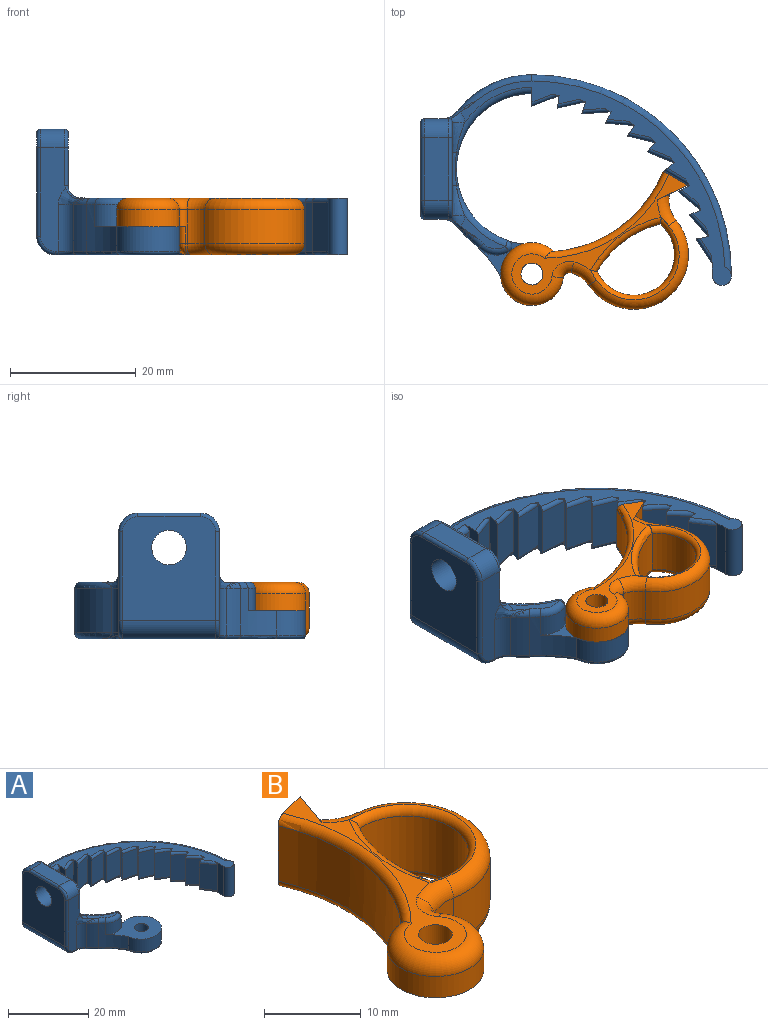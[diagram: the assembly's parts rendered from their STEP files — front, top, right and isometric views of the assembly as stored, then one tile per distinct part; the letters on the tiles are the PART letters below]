
ASSEMBLY  parts=2 mates=1
PART A: 117 faces, bbox 52.8x40.3x23.9 mm
  f0: plane 43.39x32.88mm, normal (0,0,1), area 133.2mm2, adj f5,f7,f8,f10,f11,f13,f14,f16
  f1: plane 16.41x4.05mm, normal (0,-1,0), area 52.5mm2, adj f64,f65,f67,f75,f76,f77,f85,f116
  f2: cylinder r=15mm len=7.4mm, axis (0,0,-1), area 22.7mm2, adj f3,f55,f64,f73
  f3: cylinder r=19.35mm len=7.4mm, axis (0,0,-1), area 35.4mm2, adj f2,f43,f44,f45,f56,f72
  f4: cylinder r=12mm len=23.91mm, axis (0,0,-1), area 259.4mm2, adj f5,f43,f44,f46,f50,f51,f52,f70
  f5: plane 9.1x3.1mm, normal (-1,0,0), area 18.1mm2, adj f0,f4,f6,f41,f50,f70,f98,f108
  f6: plane 7.8x4.3mm, normal (0.36,-0.93,0), area 36mm2, adj f5,f7,f98,f108
  f7: plane 9.44x1.65mm, normal (-0.15,-0.99,0), area 0.5mm2, adj f0,f6,f8,f41,f98,f108
  f8: plane 9.1x2.08mm, normal (-0.99,0.15,0), area 17.8mm2, adj f0,f7,f9,f41,f99,f109
  f9: plane 7.8x4.5mm, normal (0.22,-0.98,0), area 36mm2, adj f8,f10,f99,f109
  f10: plane 9.44x1.61mm, normal (-0.3,-0.95,0), area 0.5mm2, adj f0,f9,f11,f41,f99,f109
  f11: plane 9.1x2.01mm, normal (-0.95,0.3,0), area 17.8mm2, adj f0,f10,f12,f41,f90,f100
  f12: plane 7.8x4.6mm, normal (0.07,-1,0), area 36mm2, adj f11,f13,f90,f100
  f13: plane 9.44x1.54mm, normal (-0.44,-0.9,0), area 0.5mm2, adj f0,f12,f14,f41,f90,f100
  f14: plane 9.1x1.9mm, normal (-0.9,0.44,0), area 17.8mm2, adj f0,f13,f15,f41,f91,f101
  f15: plane 7.8x4.6mm, normal (-0.08,-1,0), area 36mm2, adj f14,f16,f91,f101
  f16: plane 9.44x1.45mm, normal (-0.57,-0.82,0), area 0.5mm2, adj f0,f15,f17,f41,f91,f101
  f17: plane 9.1x1.74mm, normal (-0.82,0.57,0), area 17.8mm2, adj f0,f16,f18,f41,f92,f102
  f18: plane 7.8x4.49mm, normal (-0.23,-0.97,0), area 36mm2, adj f17,f19,f92,f102
  f19: plane 9.44x1.33mm, normal (-0.69,-0.73,0), area 0.5mm2, adj f0,f18,f20,f41,f92,f102
  f20: plane 9.1x1.55mm, normal (-0.73,0.69,0), area 17.8mm2, adj f0,f19,f21,f41,f93,f103
  f21: plane 7.8x4.28mm, normal (-0.38,-0.93,0), area 36mm2, adj f20,f22,f93,f103
  f22: plane 9.44x1.4mm, normal (-0.79,-0.62,0), area 0.5mm2, adj f0,f21,f23,f41,f93,f103
  f23: plane 9.1x1.67mm, normal (-0.62,0.79,0), area 17.8mm2, adj f0,f22,f24,f41,f94,f104
  f24: plane 7.8x3.97mm, normal (-0.51,-0.86,0), area 36mm2, adj f23,f25,f94,f104
  f25: plane 9.44x1.51mm, normal (-0.87,-0.49,0), area 0.5mm2, adj f0,f24,f26,f41,f94,f104
  f26: plane 9.1x1.84mm, normal (-0.49,0.87,0), area 17.8mm2, adj f0,f25,f27,f41,f95,f105
  f27: plane 7.8x3.57mm, normal (-0.63,-0.77,0), area 36mm2, adj f26,f28,f95,f105
  f28: plane 9.44x1.58mm, normal (-0.94,-0.35,0), area 0.5mm2, adj f0,f27,f29,f41,f95,f105
  f29: plane 9.1x1.97mm, normal (-0.35,0.94,0), area 17.8mm2, adj f0,f28,f30,f41,f96,f106
  f30: plane 7.8x3.43mm, normal (-0.74,-0.67,0), area 36mm2, adj f29,f31,f96,f106
  f31: plane 9.44x1.64mm, normal (-0.98,-0.21,0), area 0.5mm2, adj f0,f30,f32,f41,f96,f106
  f32: plane 9.1x2.05mm, normal (-0.21,0.98,0), area 17.8mm2, adj f0,f31,f33,f41,f97,f107
  f33: plane 7.8x3.86mm, normal (-0.84,-0.55,0), area 36mm2, adj f32,f34,f97,f107
  f34: cylinder r=28.69mm len=9mm, axis (0,0,-1), area 18.6mm2, adj f0,f33,f35,f41,f97,f107
  f35: cylinder r=1.5mm len=9mm, axis (0,0,-1), area 44.9mm2, adj f0,f34,f36,f41,f57,f59
  f36: cylinder r=31.69mm len=31.94mm, axis (0,0,-1), area 350.2mm2, adj f35,f37,f57,f59
  f37: cylinder r=15mm len=11.87mm, axis (0,0,-1), area 95.9mm2, adj f36,f58,f60,f62
  f38: plane 16.41x4.05mm, normal (0,1,0), area 52.5mm2, adj f61,f62,f63,f68,f81,f82,f83,f89
  f39: plane 16.4x14.8mm, normal (-1,0,0), area 216.5mm2, adj f49,f69,f77,f78,f79,f80,f81
  f40: plane 7.13x5.3mm, normal (0,0,1), area 8.6mm2, adj f52,f54,f56,f65,f66,f115,f116
  f41: plane 46.99x35.7mm, normal (0,0,-1), area 258.7mm2, adj f5,f7,f8,f10,f11,f13,f14,f16
  f42: cylinder r=1.75mm len=4.5mm, axis (0,0,-1), area 49.5mm2, adj f41,f44
  f43: cylinder r=5mm len=10mm, axis (0,0,-1), area 96.1mm2, adj f3,f4,f44,f71
  f44: plane 13.45x10.33mm, normal (0,0,1), area 75.3mm2, adj f3,f4,f42,f43,f45,f46
  f45: cylinder r=4mm len=4.75mm, axis (0,0,-1), area 18mm2, adj f3,f44,f46,f54
  f46: cylinder r=1mm len=3.5mm, axis (0,0,1), area 8.1mm2, adj f4,f44,f45,f53
  f47: plane 14.81x9.44mm, normal (1,0,0), area 105.9mm2, adj f49,f85,f86,f87,f88,f89,f111,f112
  f48: plane 10x3.8mm, normal (0,0,1), area 38mm2, adj f67,f68,f79,f87
  f49: cylinder r=2.75mm len=5.5mm, axis (1,0,0), area 86.4mm2, adj f39,f47
  f50: torus R=13mm, axis (0,0,1), area 24.4mm2, adj f0,f4,f5,f51,f112
  f51: bspline ~6.69x1.16mm, area 3.8mm2, adj f4,f50,f52,f113
  f52: torus R=13mm, axis (0,0,1), area 18mm2, adj f4,f40,f51,f53,f114
  f53: sphere r=1mm, area 1.9mm2, adj f46,f52,f54
  f54: torus R=3mm, axis (0,0,1), area 7.3mm2, adj f40,f45,f53,f56
  f55: torus R=14mm, axis (0,0,1), area 2.2mm2, adj f2,f56,f65
  f56: torus R=20.35mm, axis (0,0,1), area 2.8mm2, adj f3,f40,f54,f55,f66
  f57: torus R=30.69mm, axis (0,0,1), area 76.6mm2, adj f35,f36,f41,f58
  f58: torus R=14mm, axis (0,0,1), area 19.3mm2, adj f37,f41,f57,f63
  f59: torus R=30.69mm, axis (0,0,1), area 76.6mm2, adj f0,f35,f36,f60
  f60: torus R=14mm, axis (0,0,1), area 19.3mm2, adj f0,f37,f59,f61
  f61: bspline ~6.49x4.52mm, area 6.6mm2, adj f0,f38,f60,f62,f110
  f62: cylinder r=3mm len=7mm, axis (0,0,-1), area 19.2mm2, adj f37,f38,f61,f63
  f63: bspline ~6.49x4.52mm, area 1.8mm2, adj f38,f58,f62,f84
  f64: cylinder r=3mm len=7.4mm, axis (0,0,-1), area 20.3mm2, adj f1,f2,f65,f74
  f65: bspline ~5.43x4.74mm, area 5.6mm2, adj f1,f40,f55,f64,f66,f116
  f66: bspline ~3.52x3.49mm, area 0mm2, adj f40,f56,f65
  f67: cylinder r=3mm len=3.8mm, axis (-1,0,0), area 17.9mm2, adj f1,f48,f78,f86
  f68: cylinder r=3mm len=3.8mm, axis (1,0,0), area 17.9mm2, adj f38,f48,f80,f88
  f69: cylinder r=3mm len=14.8mm, axis (0,-1,0), area 69.7mm2, adj f39,f41,f76,f82
  f70: torus R=12.6mm, axis (0,0,1), area 34.8mm2, adj f4,f5,f41,f71
  f71: torus R=4.4mm, axis (0,0,1), area 22.3mm2, adj f41,f43,f70,f72
  f72: torus R=19.95mm, axis (0,0,1), area 7.2mm2, adj f3,f41,f71,f73
  f73: torus R=14.4mm, axis (0,0,1), area 2.8mm2, adj f2,f41,f72,f74
  f74: torus R=3.6mm, axis (0,0,1), area 2.8mm2, adj f41,f64,f73,f75
  f75: cylinder r=0.6mm len=0.6mm, axis (1,0,0), area 0.4mm2, adj f1,f41,f74,f76
  f76: torus R=2.4mm, axis (0,1,0), area 4.1mm2, adj f1,f69,f75,f77
  f77: cylinder r=0.6mm len=14mm, axis (0,0,-1), area 13.2mm2, adj f1,f39,f76,f78
  f78: torus R=2.4mm, axis (1,0,0), area 4.1mm2, adj f39,f67,f77,f79
  f79: cylinder r=0.6mm len=10mm, axis (0,1,0), area 9.4mm2, adj f39,f48,f78,f80
  f80: torus R=2.4mm, axis (1,0,0), area 4.1mm2, adj f39,f68,f79,f81
  f81: cylinder r=0.6mm len=14mm, axis (0,0,1), area 13.2mm2, adj f38,f39,f80,f82
  f82: torus R=2.4mm, axis (0,1,0), area 4.1mm2, adj f38,f69,f81,f83
  f83: cylinder r=0.6mm len=0.6mm, axis (-1,0,0), area 0.4mm2, adj f38,f41,f82,f84
  f84: bspline ~6.37x3.6mm, area 2.3mm2, adj f41,f63,f83
  f85: cylinder r=0.6mm len=6mm, axis (0,0,1), area 5.7mm2, adj f1,f47,f86,f116
  f86: torus R=2.4mm, axis (1,0,0), area 4.1mm2, adj f47,f67,f85,f87
  f87: cylinder r=0.6mm len=10mm, axis (0,-1,0), area 9.4mm2, adj f47,f48,f86,f88
  f88: torus R=2.4mm, axis (1,0,0), area 4.1mm2, adj f47,f68,f87,f89
  f89: cylinder r=0.6mm len=6mm, axis (0,0,-1), area 5.7mm2, adj f38,f47,f88,f110
  f90: cylinder r=0.6mm len=4.65mm, axis (1,0.07,0), area 3.7mm2, adj f11,f12,f13,f41
  f91: cylinder r=0.6mm len=4.65mm, axis (1,-0.08,0), area 3.7mm2, adj f14,f15,f16,f41
  f92: cylinder r=0.6mm len=4.63mm, axis (0.97,-0.23,0), area 3.7mm2, adj f17,f18,f19,f41
  f93: cylinder r=0.6mm len=4.5mm, axis (0.93,-0.38,0), area 3.7mm2, adj f20,f21,f22,f41
  f94: cylinder r=0.6mm len=4.27mm, axis (0.86,-0.51,0), area 3.7mm2, adj f23,f24,f25,f41
  f95: cylinder r=0.6mm len=3.95mm, axis (0.77,-0.63,0), area 3.7mm2, adj f26,f27,f28,f41
  f96: cylinder r=0.6mm len=3.83mm, axis (0.67,-0.74,0), area 3.7mm2, adj f29,f30,f31,f41
  f97: cylinder r=0.6mm len=4.19mm, axis (0.55,-0.84,0), area 3.7mm2, adj f32,f33,f34,f41
  f98: cylinder r=0.6mm len=4.52mm, axis (0.93,0.36,0), area 3.7mm2, adj f5,f6,f7,f41
  f99: cylinder r=0.6mm len=4.63mm, axis (0.98,0.22,0), area 3.7mm2, adj f8,f9,f10,f41
  f100: cylinder r=0.6mm len=4.65mm, axis (-1,-0.07,0), area 3.7mm2, adj f0,f11,f12,f13
  f101: cylinder r=0.6mm len=4.65mm, axis (-1,0.08,0), area 3.7mm2, adj f0,f14,f15,f16
  f102: cylinder r=0.6mm len=4.63mm, axis (-0.97,0.23,0), area 3.7mm2, adj f0,f17,f18,f19
  f103: cylinder r=0.6mm len=4.5mm, axis (-0.93,0.38,0), area 3.7mm2, adj f0,f20,f21,f22
  f104: cylinder r=0.6mm len=4.27mm, axis (-0.86,0.51,0), area 3.7mm2, adj f0,f23,f24,f25
  f105: cylinder r=0.6mm len=3.95mm, axis (-0.77,0.63,0), area 3.7mm2, adj f0,f26,f27,f28
  f106: cylinder r=0.6mm len=3.83mm, axis (-0.67,0.74,0), area 3.7mm2, adj f0,f29,f30,f31
  f107: cylinder r=0.6mm len=4.19mm, axis (-0.55,0.84,0), area 3.7mm2, adj f0,f32,f33,f34
  f108: cylinder r=0.6mm len=4.52mm, axis (-0.93,-0.36,0), area 3.7mm2, adj f0,f5,f6,f7
  f109: cylinder r=0.6mm len=4.63mm, axis (-0.98,-0.22,0), area 3.7mm2, adj f0,f8,f9,f10
  f110: torus R=2.6mm, axis (0,0,1), area 3.4mm2, adj f0,f38,f61,f89,f111
  f111: cylinder r=2mm len=2mm, axis (0,-1,0), area 0mm2, adj f0,f47,f110,f112
  f112: bspline ~5.75x2.29mm, area 11.4mm2, adj f47,f50,f111,f113
  f113: bspline ~6.41x1.62mm, area 7.5mm2, adj f47,f51,f112,f114
  f114: bspline ~6.02x2.3mm, area 11.4mm2, adj f47,f52,f113,f115
  f115: cylinder r=2mm len=2mm, axis (0,-1,0), area 0mm2, adj f40,f47,f114,f116
  f116: torus R=2.6mm, axis (0,0,1), area 3.4mm2, adj f1,f40,f65,f85,f115
PART B: 38 faces, bbox 24.2x33.1x9.1 mm
  f0: cylinder r=20.2mm len=21.49mm, axis (0,0,-1), area 153.2mm2, adj f5,f11,f12,f15,f16,f20,f31,f32
  f1: cylinder r=5mm len=2.7mm, axis (0,0,-1), area 3.7mm2, adj f12,f16,f23,f30
  f2: cylinder r=8.67mm len=17.29mm, axis (0,0,-1), area 151.2mm2, adj f13,f14,f26,f35
  f3: cylinder r=14.41mm len=5.4mm, axis (0,0,-1), area 1.3mm2, adj f4,f13,f24,f37
  f4: plane 9.03x5.04mm, normal (0.94,-0.34,0), area 30.7mm2, adj f3,f5,f8,f9,f24,f25,f36,f37
  f5: plane 9x4.39mm, normal (-0.26,0.97,0), area 40.4mm2, adj f0,f4,f8,f9,f15,f20
  f6: cylinder r=6.42mm len=12.85mm, axis (0,0,-1), area 161.5mm2, adj f7,f18,f21
  f7: cylinder r=16.13mm len=12.39mm, axis (0,0,-1), area 90mm2, adj f6,f19,f22
  f8: plane 30.66x11.39mm, normal (0,0,1), area 54.2mm2, adj f4,f5,f10,f20,f22,f32,f33,f34
  f9: plane 21.47x5.9mm, normal (0,0,-1), area 27mm2, adj f4,f5,f15,f19,f25,f27,f28,f30
  f10: cylinder r=1.75mm len=4.5mm, axis (0,0,-1), area 49.5mm2, adj f8,f12
  f11: cylinder r=5mm len=10mm, axis (0,0,-1), area 72.3mm2, adj f0,f12,f17,f32
  f12: plane 11.31x10mm, normal (0,0,-1), area 69.8mm2, adj f0,f1,f10,f11,f16,f17,f23
  f13: cylinder r=5mm len=5.4mm, axis (0,0,1), area 22.6mm2, adj f2,f3,f25,f36
  f14: cylinder r=5mm len=5.4mm, axis (0,0,1), area 19.2mm2, adj f2,f17,f27,f34
  f15: torus R=21.2mm, axis (0,0,1), area 32.3mm2, adj f0,f5,f9,f31
  f16: cylinder r=1mm len=2.7mm, axis (0,0,-1), area 5.1mm2, adj f0,f1,f12,f31
  f17: cylinder r=1mm len=5.4mm, axis (0,0,-1), area 5.4mm2, adj f11,f12,f14,f23,f28,f33
  f18: torus R=7.42mm, axis (0,0,1), area 32.6mm2, adj f6,f19,f25,f26,f27
  f19: torus R=17.13mm, axis (0,0,1), area 21.2mm2, adj f7,f9,f18,f25,f27
  f20: torus R=21.2mm, axis (0,0,1), area 37.7mm2, adj f0,f5,f8,f32
  f21: torus R=7.42mm, axis (0,0,1), area 32.6mm2, adj f6,f22,f34,f35,f36
  f22: torus R=17.13mm, axis (0,0,1), area 21.2mm2, adj f7,f8,f21,f34,f36
  f23: cylinder r=1mm len=2.7mm, axis (0,0,1), area 3.8mm2, adj f1,f12,f17,f29
  f24: torus R=12.61mm, axis (0,0,1), area 0.2mm2, adj f3,f4,f25
  f25: torus R=6.8mm, axis (0,0,1), area 12.2mm2, adj f4,f9,f13,f18,f19,f24,f26
  f26: torus R=6.87mm, axis (0,0,1), area 65.9mm2, adj f2,f18,f25,f27
  f27: torus R=6.8mm, axis (0,0,1), area 11mm2, adj f9,f14,f18,f19,f26,f28
  f28: torus R=2.8mm, axis (0,0,1), area 0.8mm2, adj f9,f17,f27,f29
  f29: bspline ~2.28x2.26mm, area 2.4mm2, adj f23,f28,f30
  f30: torus R=6.8mm, axis (0,0,1), area 3.6mm2, adj f1,f9,f29,f31
  f31: bspline ~2.52x2.29mm, area 4.1mm2, adj f0,f15,f16,f30
  f32: torus R=3.2mm, axis (0,0,1), area 65.1mm2, adj f0,f8,f11,f20,f33
  f33: torus R=2.8mm, axis (0,0,1), area 8mm2, adj f8,f17,f32,f34
  f34: torus R=6.8mm, axis (0,0,1), area 11mm2, adj f8,f14,f21,f22,f33,f35
  f35: torus R=6.87mm, axis (0,0,1), area 65.9mm2, adj f2,f21,f34,f36
  f36: torus R=6.8mm, axis (0,0,1), area 12.2mm2, adj f4,f8,f13,f21,f22,f35,f37
  f37: torus R=12.61mm, axis (0,0,1), area 0.2mm2, adj f3,f4,f36
PLACE A rot(axis=(0.02,1,-0.07),0deg) t=(33.03,101.49,16.21)mm
PLACE B rot(axis=(0,0,-1),44.8deg) t=(67.73,45.69,16.21)mm
MATE revolute A.f36 <-> B.f1  axis (0,0,1) through (33.03,84.8,20.71)mm
